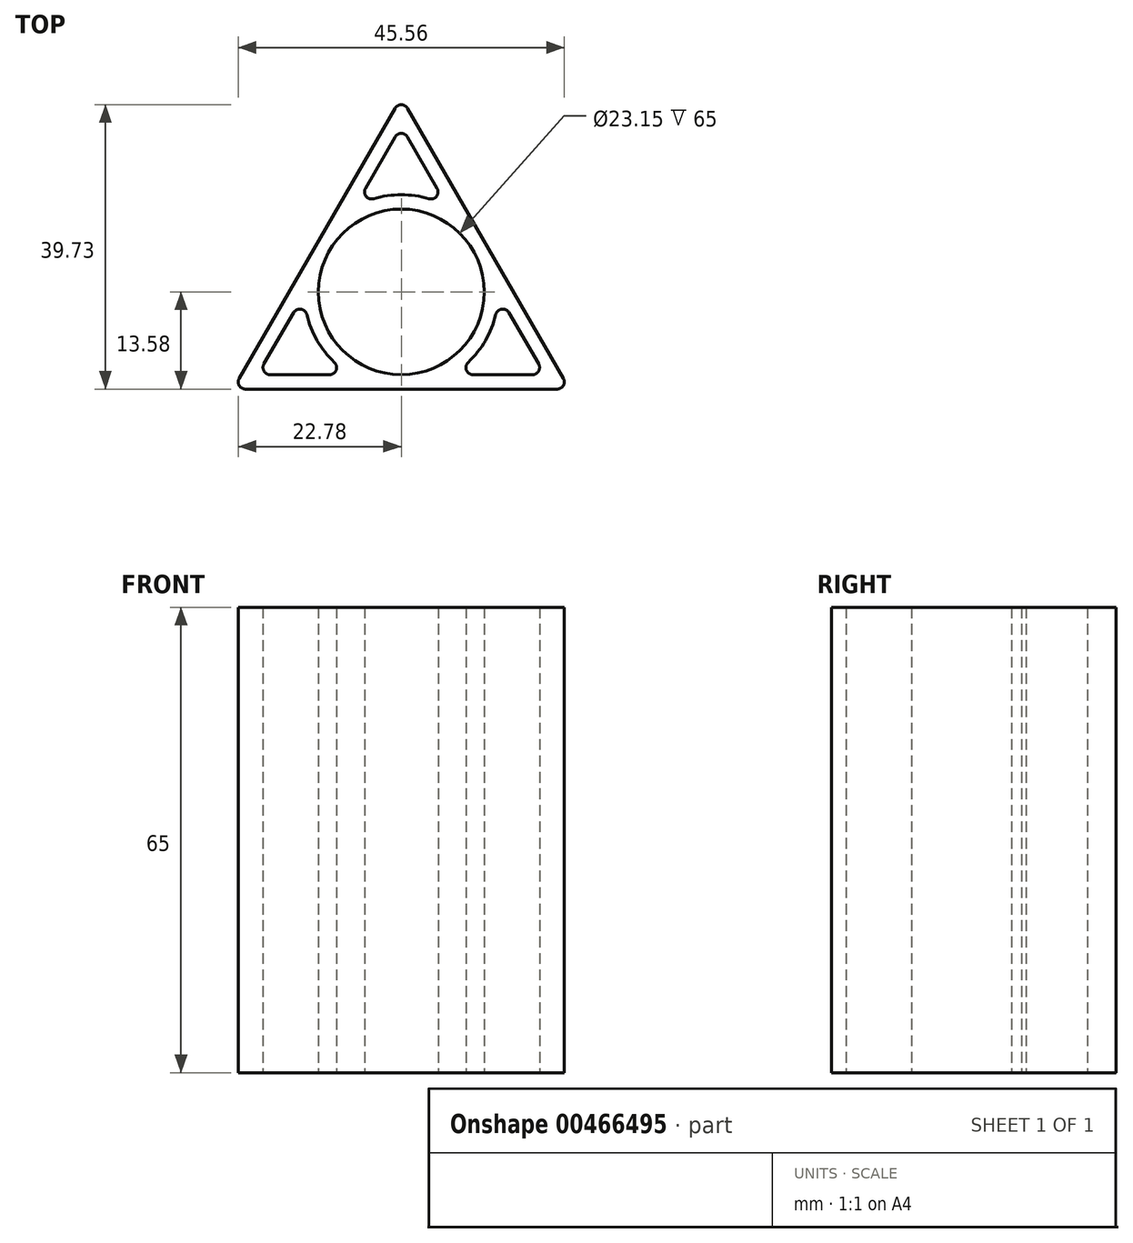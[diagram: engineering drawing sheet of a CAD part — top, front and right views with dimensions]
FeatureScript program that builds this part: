
annotation { "Feature Type Name" : "Feature", "Feature Type Description" : "" }
export const myFeature = defineFeature(function(context is Context, id is Id, definition is map)
    precondition{}
    {
        {
            var Q0;
            Q0=qCreatedBy(makeId("Top.planeOp"),FACE);
            var sketch = newSketch(context, id + "F0", { "sketchPlane" : qUnion([Q0])});
            skCircle(sketch, "E0.cCircle", {"center": v(0, 0) * mm, "radius": 27.15 * mm, "construction": true});
            skLineSegment(sketch, "E0.0", {"start": v(0.87, 25.65) * mm, "end": v(11.76, 6.79) * mm});
            skLineSegment(sketch, "E0.1", {"start": v(21.78, -13.57) * mm, "end": v(-21.78, -13.58) * mm});
            skLineSegment(sketch, "E0.2", {"start": v(-22.65, -12.08) * mm, "end": v(-0.87, 25.65) * mm});
            skLineSegment(sketch, "E1.0", {"start": v(-19.18, -10.08) * mm, "end": v(-15.04, -2.9) * mm});
            skLineSegment(sketch, "E1.1", {"start": v(18.32, -11.57) * mm, "end": v(10.03, -11.57) * mm});
            skLineSegment(sketch, "E1.2", {"start": v(0.87, 21.65) * mm, "end": v(5, 14.47) * mm});
            skCircle(sketch, "E2.0", {"center": v(0, 0) * mm, "radius": 11.57 * mm});
            skLineSegment(sketch, "E3", {"start": v(6.48, 11.93) * mm, "end": v(13.57, -0.35) * mm, "construction": true});
            skLineSegment(sketch, "E4", {"start": v(15.04, -2.9) * mm, "end": v(19.18, -10.07) * mm});
            skLineSegment(sketch, "E5", {"start": v(11.76, 6.79) * mm, "end": v(22.65, -12.07) * mm});
            skArc(sketch, "E6", {"start": v(3.86, 13.01) * mm, "mid": v(0, 13.57) * mm, "end": v(-3.86, 13.01) * mm});
            skArc(sketch, "E7", {"start": v(13.57, -0.35) * mm, "mid": v(11.76, 6.79) * mm, "end": v(6.48, 11.93) * mm, "construction": true});
            skLineSegment(sketch, "E8", {"start": v(-5, 14.47) * mm, "end": v(-0.87, 21.65) * mm});
            skLineSegment(sketch, "E9", {"start": v(-13.57, -0.35) * mm, "end": v(-6.48, 11.93) * mm, "construction": true});
            skArc(sketch, "E10", {"start": v(-6.48, 11.93) * mm, "mid": v(-11.76, 6.79) * mm, "end": v(-13.57, -0.35) * mm, "construction": true});
            skArc(sketch, "E11", {"start": v(-13.2, -3.17) * mm, "mid": v(-11.76, -6.79) * mm, "end": v(-9.34, -9.85) * mm});
            skLineSegment(sketch, "E12", {"start": v(-10.03, -11.57) * mm, "end": v(-18.32, -11.57) * mm});
            skLineSegment(sketch, "E13", {"start": v(7.1, -11.57) * mm, "end": v(-7.1, -11.57) * mm, "construction": true});
            skArc(sketch, "E14", {"start": v(9.34, -9.85) * mm, "mid": v(11.76, -6.79) * mm, "end": v(13.2, -3.17) * mm});
            skArc(sketch, "E15", {"start": v(-7.1, -11.57) * mm, "mid": v(0, -13.57) * mm, "end": v(7.1, -11.57) * mm, "construction": true});
            skPoint(sketch, "E16.visualSharp", {"position": v(0, 27.15) * mm});
            skArc(sketch, "E16.filletArc", {"start": v(0.87, 25.65) * mm, "mid": v(0, 26.15) * mm, "end": v(-0.87, 25.65) * mm});
            skCircle(sketch, "E17", {"center": v(0, 0) * mm, "radius": 26.15 * mm, "construction": true});
            skPoint(sketch, "E18.visualSharp", {"position": v(23.51, -13.57) * mm});
            skArc(sketch, "E18.filletArc", {"start": v(21.78, -13.57) * mm, "mid": v(22.65, -13.07) * mm, "end": v(22.65, -12.07) * mm});
            skPoint(sketch, "E19.visualSharp", {"position": v(-23.51, -13.58) * mm});
            skArc(sketch, "E19.filletArc", {"start": v(-22.65, -12.08) * mm, "mid": v(-22.65, -13.08) * mm, "end": v(-21.78, -13.58) * mm});
            skPoint(sketch, "E20.visualSharp", {"position": v(-20.05, -11.57) * mm});
            skArc(sketch, "E20.filletArc", {"start": v(-19.18, -10.07) * mm, "mid": v(-19.18, -11.07) * mm, "end": v(-18.32, -11.57) * mm});
            skPoint(sketch, "E21.visualSharp", {"position": v(20.05, -11.57) * mm});
            skArc(sketch, "E21.filletArc", {"start": v(18.32, -11.57) * mm, "mid": v(19.18, -11.07) * mm, "end": v(19.18, -10.07) * mm});
            skPoint(sketch, "E22.visualSharp", {"position": v(0, 23.15) * mm});
            skArc(sketch, "E22.filletArc", {"start": v(0.87, 21.65) * mm, "mid": v(0, 22.15) * mm, "end": v(-0.87, 21.65) * mm});
            skPoint(sketch, "E23.visualSharp", {"position": v(-13.57, -0.35) * mm});
            skArc(sketch, "E23.filletArc", {"start": v(-13.2, -3.17) * mm, "mid": v(-14.03, -2.4) * mm, "end": v(-15.04, -2.9) * mm});
            skPoint(sketch, "E24.visualSharp", {"position": v(-7.1, -11.57) * mm});
            skArc(sketch, "E24.filletArc", {"start": v(-10.03, -11.57) * mm, "mid": v(-9.1, -10.95) * mm, "end": v(-9.34, -9.85) * mm});
            skPoint(sketch, "E25.visualSharp", {"position": v(7.1, -11.57) * mm});
            skArc(sketch, "E25.filletArc", {"start": v(9.34, -9.85) * mm, "mid": v(9.1, -10.95) * mm, "end": v(10.03, -11.57) * mm});
            skPoint(sketch, "E26.visualSharp", {"position": v(13.57, -0.35) * mm});
            skArc(sketch, "E26.filletArc", {"start": v(15.04, -2.9) * mm, "mid": v(14.03, -2.4) * mm, "end": v(13.2, -3.17) * mm});
            skPoint(sketch, "E27.visualSharp", {"position": v(6.48, 11.93) * mm});
            skArc(sketch, "E27.filletArc", {"start": v(3.86, 13.01) * mm, "mid": v(4.93, 13.35) * mm, "end": v(5, 14.47) * mm});
            skPoint(sketch, "E28.visualSharp", {"position": v(-6.48, 11.93) * mm});
            skArc(sketch, "E28.filletArc", {"start": v(-5, 14.47) * mm, "mid": v(-4.93, 13.35) * mm, "end": v(-3.86, 13.01) * mm});
            skSolve(sketch);
        }
        {
            var Q0;
            Q0=makeQuery(id+"F0.imprint","IMPRINT",FACE,{"disambiguationData":[TD([[makeQuery(id+"F0.imprint","IMPRINT",EDGE,{"derivedFrom":sQuery(id+"F0.wireOp",EDGE,"E0.0")}),-1.0]])]});
            extrude(context, id + "F1", {"entities" : qUnion([Q0]), "offsetDistance" : 25 * mm, "depth" : 65 * mm});
        }
    });
